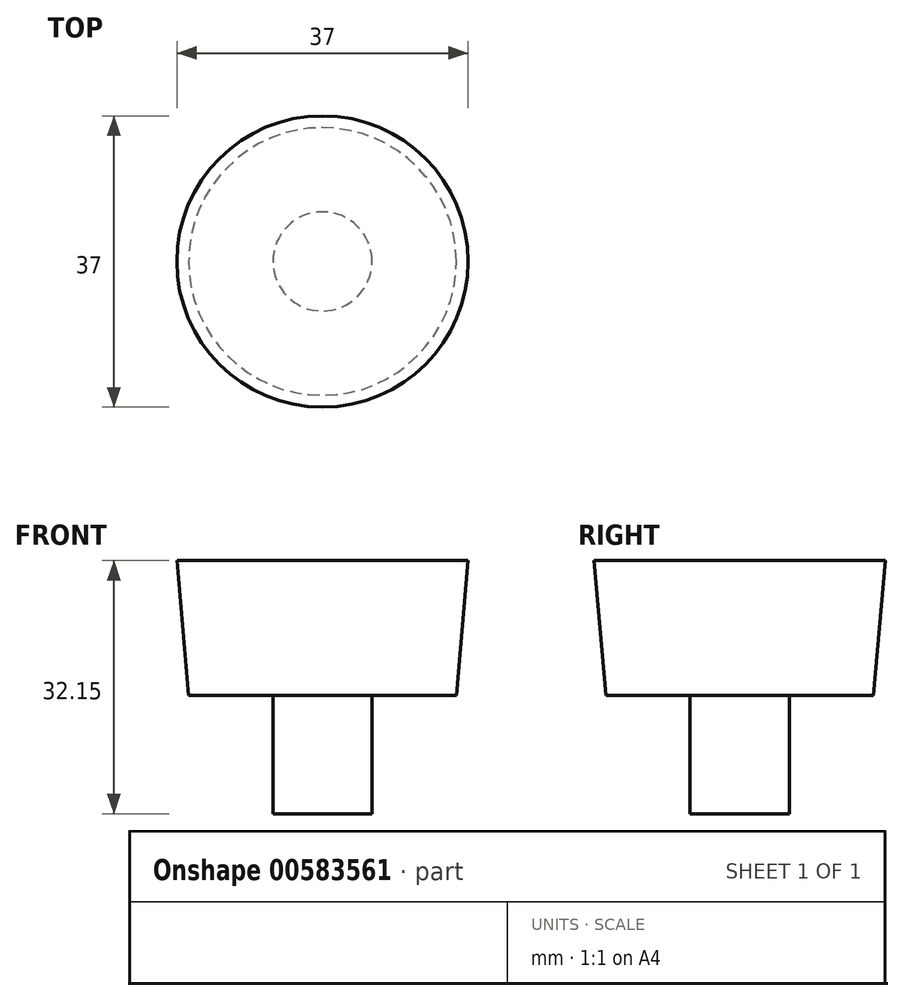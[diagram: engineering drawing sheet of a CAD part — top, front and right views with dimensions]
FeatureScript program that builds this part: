
annotation { "Feature Type Name" : "Feature", "Feature Type Description" : "" }
export const myFeature = defineFeature(function(context is Context, id is Id, definition is map)
    precondition{}
    {
        {
            var Q0;
            Q0=qCreatedBy(makeId("Top.planeOp"),FACE);
            var sketch = newSketch(context, id + "F0", { "sketchPlane" : qUnion([Q0])});
            skCircle(sketch, "E0", {"center": v(0, 0) * mm, "radius": 6.3 * mm});
            skSolve(sketch);
        }
        {
            var Q0;
            Q0 = qSketchRegion(id + "F0", true);
            extrude(context, id + "F1", {"entities" : qUnion([Q0]), "depth" : 15 * mm, "offsetDistance" : 25 * mm});
        }
        {
            var Q0;
            Q0=qCreatedBy(makeId("Right.planeOp"),FACE);
            var sketch = newSketch(context, id + "F2", { "sketchPlane" : qUnion([Q0])});
            skLineSegment(sketch, "E1", {"start": v(0, 0) * mm, "end": v(0, 15) * mm, "construction": true});
            skLineSegment(sketch, "E2", {"start": v(0, 15) * mm, "end": v(17, 15) * mm});
            skLineSegment(sketch, "E3", {"start": v(0, 15) * mm, "end": v(0, 32.15) * mm, "construction": true});
            skLineSegment(sketch, "E4", {"start": v(0, 32.15) * mm, "end": v(18.5, 32.15) * mm});
            skLineSegment(sketch, "E5", {"start": v(18.5, 32.15) * mm, "end": v(17, 15) * mm});
            skLineSegment(sketch, "E6", {"start": v(0, 32.15) * mm, "end": v(0, 15) * mm});
            skSolve(sketch);
        }
        {
            var Q0;
            Q0 = qSketchRegion(id + "F2", true);
            var Q1;
            Q1=sQuery(id+"F2.wireOp",EDGE,"E1");
            revolve(context, id + "F3", {"operationType" : NewBodyOperationType.ADD, "entities" : qUnion([Q0]), "axis" : qUnion([Q1]), "revolveType" : RevolveType.FULL});
        }
    });
